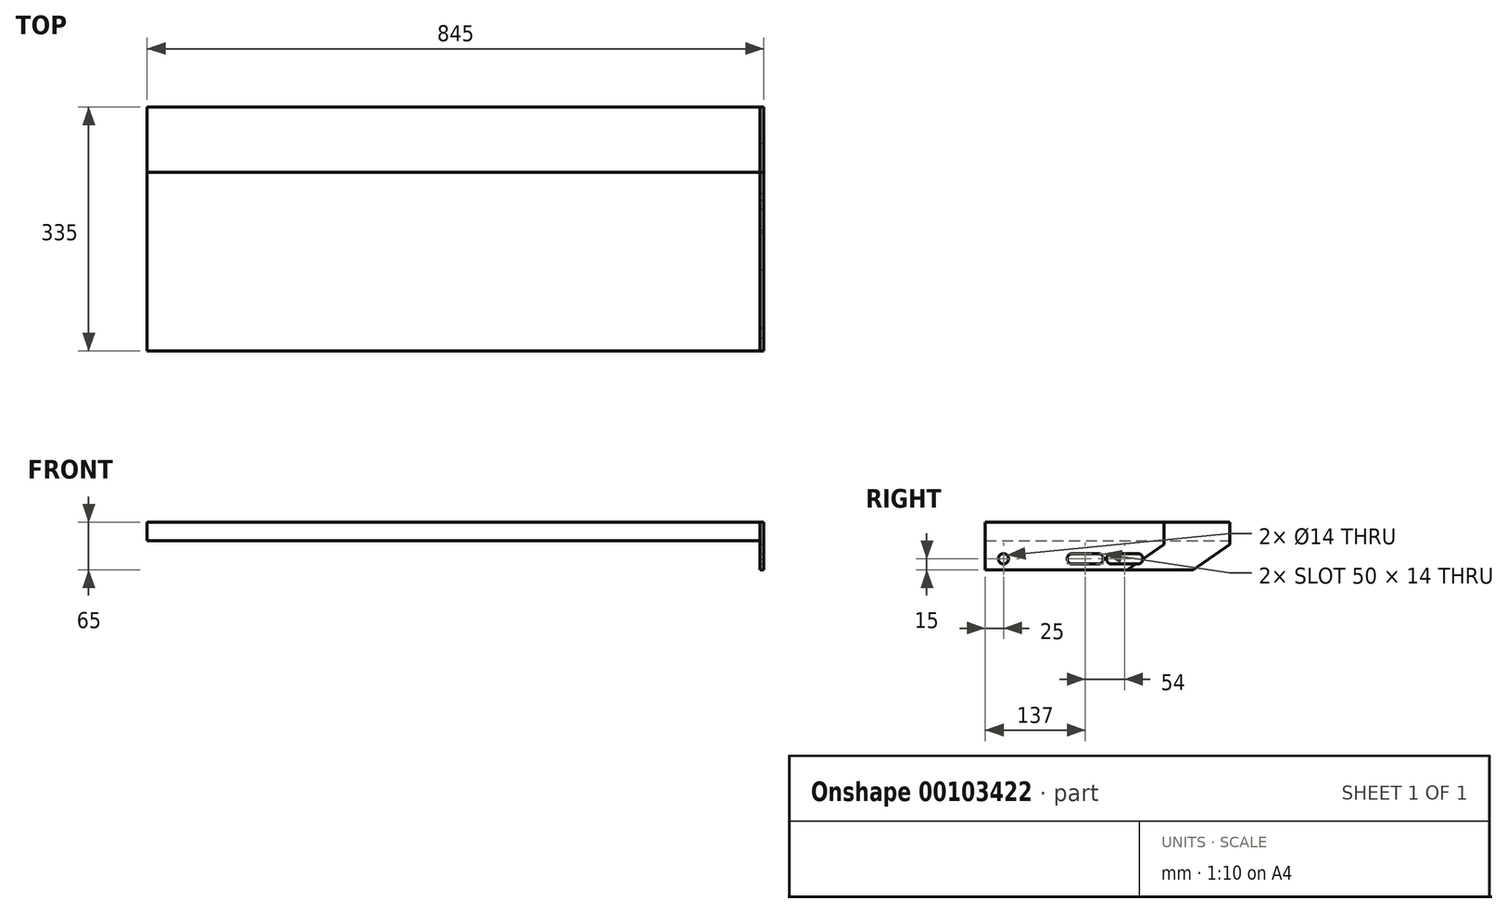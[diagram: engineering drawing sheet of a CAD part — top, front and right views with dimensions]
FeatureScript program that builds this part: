
annotation { "Feature Type Name" : "Feature", "Feature Type Description" : "" }
export const myFeature = defineFeature(function(context is Context, id is Id, definition is map)
    precondition{}
    {
        {
            var Q0;
            Q0=qCreatedBy(makeId("Top.planeOp"),FACE);
            var sketch = newSketch(context, id + "F0", { "sketchPlane" : qUnion([Q0])});
            skLineSegment(sketch, "E0.bottom", {"start": v(-420, 0) * mm, "end": v(420, 0) * mm});
            skLineSegment(sketch, "E0.top", {"start": v(-420, 245) * mm, "end": v(420, 245) * mm});
            skLineSegment(sketch, "E0.left", {"start": v(-420, 0) * mm, "end": v(-420, 245) * mm});
            skLineSegment(sketch, "E0.right", {"start": v(420, 0) * mm, "end": v(420, 245) * mm});
            skSolve(sketch);
        }
        {
            var Q0;
            Q0 = qSketchRegion(id + "F0", true);
            extrude(context, id + "F1", {"entities" : qUnion([Q0]), "oppositeDirection" : true, "depth" : 25 * mm, "offsetDistance" : 25 * mm});
        }
        {
            var Q0;
            Q0=makeQuery(id+"F1.opExtrude","SWEPT_FACE",FACE,{"disambiguationData":[OSD([sQuery(id+"F0.wireOp",EDGE,"E0.right")])]});
            var sketch = newSketch(context, id + "F2", { "sketchPlane" : qUnion([Q0])});
            skLineSegment(sketch, "E1.bottom", {"start": v(0, 0) * mm, "end": v(245, 0) * mm});
            skLineSegment(sketch, "E1.top", {"start": v(0, -65) * mm, "end": v(245, -65) * mm});
            skLineSegment(sketch, "E1.left", {"start": v(0, 0) * mm, "end": v(0, -65) * mm});
            skLineSegment(sketch, "E1.right", {"start": v(245, 0) * mm, "end": v(245, -65) * mm});
            skSolve(sketch);
        }
        {
            var Q0;
            Q0 = qSketchRegion(id + "F2", true);
            extrude(context, id + "F3", {"entities" : qUnion([Q0]), "depth" : 5 * mm, "offsetDistance" : 25 * mm});
        }
        {
            var Q0;
            Q0=makeQuery(id+"F3.opExtrude","SWEPT_EDGE",EDGE,{"disambiguationData":[OSD([sQuery(id+"F2.wireOp",EDGE,"E1.top"),sQuery(id+"F2.wireOp",EDGE,"E1.right")])]});
            chamfer(context, id + "F4", {"entities" : qUnion([Q0]), "chamferType" : ChamferType.OFFSET_ANGLE, "width" : 50 * mm, "oppositeDirection" : true, "angle" : 35 * degree, "tangentPropagation" : true});
        }
        {
            var Q0;
            Q0=makeQuery(id+"F3.opExtrude","CAP_FACE",FACE,{"disambiguationData":[OSD([sQuery(id+"F2.wireOp",EDGE,"E1.bottom"),sQuery(id+"F2.wireOp",EDGE,"E1.top"),sQuery(id+"F2.wireOp",EDGE,"E1.left"),sQuery(id+"F2.wireOp",EDGE,"E1.right")])],"isStart":false});
            var sketch = newSketch(context, id + "F5", { "sketchPlane" : qUnion([Q0])});
            skCircle(sketch, "E2", {"center": v(25, -50) * mm, "radius": 7 * mm});
            skArc(sketch, "E3", {"start": v(119, -43) * mm, "mid": v(112, -50) * mm, "end": v(119, -57) * mm});
            skArc(sketch, "E4", {"start": v(155, -57) * mm, "mid": v(162, -50) * mm, "end": v(155, -43) * mm});
            skLineSegment(sketch, "E5", {"start": v(119, -43) * mm, "end": v(155, -43) * mm});
            skLineSegment(sketch, "E6", {"start": v(119, -57) * mm, "end": v(155, -57) * mm});
            skPoint(sketch, "E7", {"position": v(137, -57) * mm});
            skSolve(sketch);
        }
        {
            var Q0;
            Q0 = qSketchRegion(id + "F5", true);
            extrude(context, id + "F6", {"entities" : qUnion([Q0]), "operationType" : NewBodyOperationType.REMOVE, "oppositeDirection" : true, "depth" : 25 * mm, "offsetDistance" : 25 * mm});
        }
        {
            var Q0;
            Q0=makeQuery(id+"F3.opExtrude","SWEPT_BODY",BODY,{"disambiguationData":[OSD([sQuery(id+"F2.wireOp",EDGE,"E1.bottom"),sQuery(id+"F2.wireOp",EDGE,"E1.top"),sQuery(id+"F2.wireOp",EDGE,"E1.left"),sQuery(id+"F2.wireOp",EDGE,"E1.right")])]});
            var Q1;
            Q1=makeQuery(id+"F3.opExtrude","CAP_VERTEX",VERTEX,{"disambiguationData":[OSD([sQuery(id+"F2.wireOp",EDGE,"E1.bottom"),sQuery(id+"F2.wireOp",EDGE,"E1.left")])],"isStart":false});
            var Q2;
            Q2=makeQuery(id+"F1.opExtrude","CAP_VERTEX",VERTEX,{"disambiguationData":[OSD([sQuery(id+"F0.wireOp",EDGE,"E0.bottom"),sQuery(id+"F0.wireOp",EDGE,"E0.left")])],"isStart":true});
            transform(context, id + "F7", {"entities" : qUnion([Q0]), "transformType" : TransformType.TRANSLATION_ENTITY, "oppositeDirectionEntity" : false, "transformLine" : qUnion([Q1, Q2]), "makeCopy" : true});
        }
        {
            var Q0;
            Q0=makeQuery(id+"F1.opExtrude","SWEPT_BODY",BODY,{"disambiguationData":[OSD([sQuery(id+"F0.wireOp",EDGE,"E0.bottom"),sQuery(id+"F0.wireOp",EDGE,"E0.top"),sQuery(id+"F0.wireOp",EDGE,"E0.left"),sQuery(id+"F0.wireOp",EDGE,"E0.right")])]});
            transform(context, id + "F8", {"entities" : qUnion([Q0]), "transformType" : TransformType.TRANSLATION_3D, "dx" : 0 * mm, "dy" : 0 * mm, "dz" : 0 * mm, "makeCopy" : true});
        }
        {
            var Q0;
            Q0=makeQuery(id+"F1.opExtrude","SWEPT_BODY",BODY,{"disambiguationData":[OSD([sQuery(id+"F0.wireOp",EDGE,"E0.bottom"),sQuery(id+"F0.wireOp",EDGE,"E0.top"),sQuery(id+"F0.wireOp",EDGE,"E0.left"),sQuery(id+"F0.wireOp",EDGE,"E0.right")])]});
            deleteBodies(context, id + "F9", {"entities" : qUnion([Q0])});
        }
        {
            var Q0;
            Q0=makeQuery(id+"F3.opExtrude","SWEPT_BODY",BODY,{"disambiguationData":[OSD([sQuery(id+"F2.wireOp",EDGE,"E1.bottom"),sQuery(id+"F2.wireOp",EDGE,"E1.top"),sQuery(id+"F2.wireOp",EDGE,"E1.left"),sQuery(id+"F2.wireOp",EDGE,"E1.right")])]});
            var Q1;
            Q1=makeQuery(id+"F3.opExtrude","CAP_VERTEX",VERTEX,{"disambiguationData":[OSD([sQuery(id+"F2.wireOp",EDGE,"E1.bottom"),sQuery(id+"F2.wireOp",EDGE,"E1.left")])],"isStart":true});
            var Q2;
            Q2=makeQuery(id+"F3.opExtrude","CAP_VERTEX",VERTEX,{"disambiguationData":[OSD([sQuery(id+"F2.wireOp",EDGE,"E1.bottom"),sQuery(id+"F2.wireOp",EDGE,"E1.left")])],"isStart":false});
            transform(context, id + "F10", {"entities" : qUnion([Q0]), "transformType" : TransformType.TRANSLATION_ENTITY, "oppositeDirectionEntity" : false, "transformLine" : qUnion([Q1, Q2]), "makeCopy" : true});
        }
        {
            var Q0;
            Q0=makeQuery(id+"F8.opPattern","COPY",BODY,{"derivedFrom":makeQuery(id+"F1.opExtrude","SWEPT_BODY",BODY,{"disambiguationData":[OSD([sQuery(id+"F0.wireOp",EDGE,"E0.bottom"),sQuery(id+"F0.wireOp",EDGE,"E0.top"),sQuery(id+"F0.wireOp",EDGE,"E0.left"),sQuery(id+"F0.wireOp",EDGE,"E0.right")])]}),"instanceName":"1"});
            transform(context, id + "F11", {"entities" : qUnion([Q0]), "transformType" : TransformType.TRANSLATION_3D, "dx" : 0 * mm, "dy" : 0 * mm, "dz" : 0 * mm, "makeCopy" : true});
        }
        {
            var Q0;
            Q0=makeQuery(id+"F10.opPattern","COPY",BODY,{"derivedFrom":makeQuery(id+"F3.opExtrude","SWEPT_BODY",BODY,{"disambiguationData":[OSD([sQuery(id+"F2.wireOp",EDGE,"E1.bottom"),sQuery(id+"F2.wireOp",EDGE,"E1.top"),sQuery(id+"F2.wireOp",EDGE,"E1.left"),sQuery(id+"F2.wireOp",EDGE,"E1.right")])]}),"instanceName":"1"});
            deleteBodies(context, id + "F12", {"entities" : qUnion([Q0])});
        }
        {
            var Q0;
            Q0=makeQuery(id+"F3.opExtrude","SWEPT_BODY",BODY,{"disambiguationData":[OSD([sQuery(id+"F2.wireOp",EDGE,"E1.bottom"),sQuery(id+"F2.wireOp",EDGE,"E1.top"),sQuery(id+"F2.wireOp",EDGE,"E1.left"),sQuery(id+"F2.wireOp",EDGE,"E1.right")])]});
            transform(context, id + "F13", {"entities" : qUnion([Q0]), "transformType" : TransformType.TRANSLATION_3D, "dx" : 0 * mm, "dy" : 0 * mm, "dz" : 0 * mm, "makeCopy" : true});
        }
        {
            var Q0;
            Q0=makeQuery(id+"F3.opExtrude","SWEPT_BODY",BODY,{"disambiguationData":[OSD([sQuery(id+"F2.wireOp",EDGE,"E1.bottom"),sQuery(id+"F2.wireOp",EDGE,"E1.top"),sQuery(id+"F2.wireOp",EDGE,"E1.left"),sQuery(id+"F2.wireOp",EDGE,"E1.right")])]});
            deleteBodies(context, id + "F14", {"entities" : qUnion([Q0])});
        }
        {
            var Q0;
            Q0=makeQuery(id+"F7.opPattern","COPY",BODY,{"derivedFrom":makeQuery(id+"F3.opExtrude","SWEPT_BODY",BODY,{"disambiguationData":[OSD([sQuery(id+"F2.wireOp",EDGE,"E1.bottom"),sQuery(id+"F2.wireOp",EDGE,"E1.top"),sQuery(id+"F2.wireOp",EDGE,"E1.left"),sQuery(id+"F2.wireOp",EDGE,"E1.right")])]}),"instanceName":"1"});
            var Q1;
            Q1=makeQuery(id+"F8.opPattern","COPY",BODY,{"derivedFrom":makeQuery(id+"F1.opExtrude","SWEPT_BODY",BODY,{"disambiguationData":[OSD([sQuery(id+"F0.wireOp",EDGE,"E0.bottom"),sQuery(id+"F0.wireOp",EDGE,"E0.top"),sQuery(id+"F0.wireOp",EDGE,"E0.left"),sQuery(id+"F0.wireOp",EDGE,"E0.right")])]}),"instanceName":"1"});
            deleteBodies(context, id + "F15", {"entities" : qUnion([Q0, Q1])});
        }
        {
            var Q0;
            Q0=qCreatedBy(makeId("Right.planeOp"),FACE);
            var sketch = newSketch(context, id + "F16", { "sketchPlane" : qUnion([Q0])});
            skLineSegment(sketch, "E8.bottom", {"start": v(0, 0) * mm, "end": v(335, 0) * mm});
            skLineSegment(sketch, "E8.top", {"start": v(0, -25) * mm, "end": v(335, -25) * mm});
            skLineSegment(sketch, "E8.left", {"start": v(0, 0) * mm, "end": v(0, -25) * mm});
            skLineSegment(sketch, "E8.right", {"start": v(335, 0) * mm, "end": v(335, -25) * mm});
            skSolve(sketch);
        }
        {
            var Q0;
            Q0 = qSketchRegion(id + "F16", true);
            extrude(context, id + "F17", {"entities" : qUnion([Q0]), "depth" : 420 * mm, "offsetDistance" : 25 * mm, "hasSecondDirection" : true, "secondDirectionOppositeDirection" : true, "secondDirectionDepth" : 420 * mm});
        }
        {
            var Q0;
            Q0=makeQuery(id+"F17.opExtrude","CAP_FACE",FACE,{"disambiguationData":[OSD([sQuery(id+"F16.wireOp",EDGE,"E8.bottom"),sQuery(id+"F16.wireOp",EDGE,"E8.top"),sQuery(id+"F16.wireOp",EDGE,"E8.left"),sQuery(id+"F16.wireOp",EDGE,"E8.right")])],"isStart":false});
            var sketch = newSketch(context, id + "F18", { "sketchPlane" : qUnion([Q0])});
            skPoint(sketch, "E9.oppositeSnap0", {"position": v(335, -12.5) * mm});
            skLineSegment(sketch, "E9.bottom", {"start": v(0, 0) * mm, "end": v(335, 0) * mm});
            skLineSegment(sketch, "E9.top", {"start": v(0, -65) * mm, "end": v(335, -65) * mm});
            skLineSegment(sketch, "E9.left", {"start": v(0, 0) * mm, "end": v(0, -65) * mm});
            skLineSegment(sketch, "E9.right", {"start": v(335, 0) * mm, "end": v(335, -65) * mm});
            skSolve(sketch);
        }
        {
            var Q0;
            Q0 = qSketchRegion(id + "F18", true);
            extrude(context, id + "F19", {"entities" : qUnion([Q0]), "depth" : 5 * mm, "offsetDistance" : 25 * mm});
        }
        {
            var Q0;
            Q0=makeQuery(id+"F19.opExtrude","SWEPT_EDGE",EDGE,{"disambiguationData":[OSD([sQuery(id+"F18.wireOp",EDGE,"E9.top"),sQuery(id+"F18.wireOp",EDGE,"E9.right")])]});
            chamfer(context, id + "F20", {"entities" : qUnion([Q0]), "chamferType" : ChamferType.OFFSET_ANGLE, "width" : 50 * mm, "oppositeDirection" : true, "angle" : 35 * degree, "tangentPropagation" : true});
        }
        {
            var Q0;
            Q0=makeQuery(id+"F19.opExtrude","CAP_FACE",FACE,{"disambiguationData":[OSD([sQuery(id+"F18.wireOp",EDGE,"E9.bottom"),sQuery(id+"F18.wireOp",EDGE,"E9.top"),sQuery(id+"F18.wireOp",EDGE,"E9.left"),sQuery(id+"F18.wireOp",EDGE,"E9.right")])],"isStart":false});
            var sketch = newSketch(context, id + "F21", { "sketchPlane" : qUnion([Q0])});
            skCircle(sketch, "E10", {"center": v(25, -50) * mm, "radius": 7 * mm});
            skArc(sketch, "E11", {"start": v(173, -43) * mm, "mid": v(166, -50) * mm, "end": v(173, -57) * mm});
            skArc(sketch, "E12", {"start": v(209, -57) * mm, "mid": v(216, -50) * mm, "end": v(209, -43) * mm});
            skLineSegment(sketch, "E13", {"start": v(173, -43) * mm, "end": v(209, -43) * mm});
            skLineSegment(sketch, "E14", {"start": v(209, -57) * mm, "end": v(173, -57) * mm});
            skLineSegment(sketch, "E15", {"start": v(173, -50) * mm, "end": v(209, -50) * mm, "construction": true});
            skPoint(sketch, "E16", {"position": v(191, -50) * mm});
            skSolve(sketch);
        }
        {
            var Q0;
            Q0 = qSketchRegion(id + "F21", true);
            extrude(context, id + "F22", {"entities" : qUnion([Q0]), "operationType" : NewBodyOperationType.REMOVE, "endBound" : BoundingType.UP_TO_NEXT, "oppositeDirection" : true, "depth" : 25 * mm, "offsetDistance" : 25 * mm});
        }
    });
